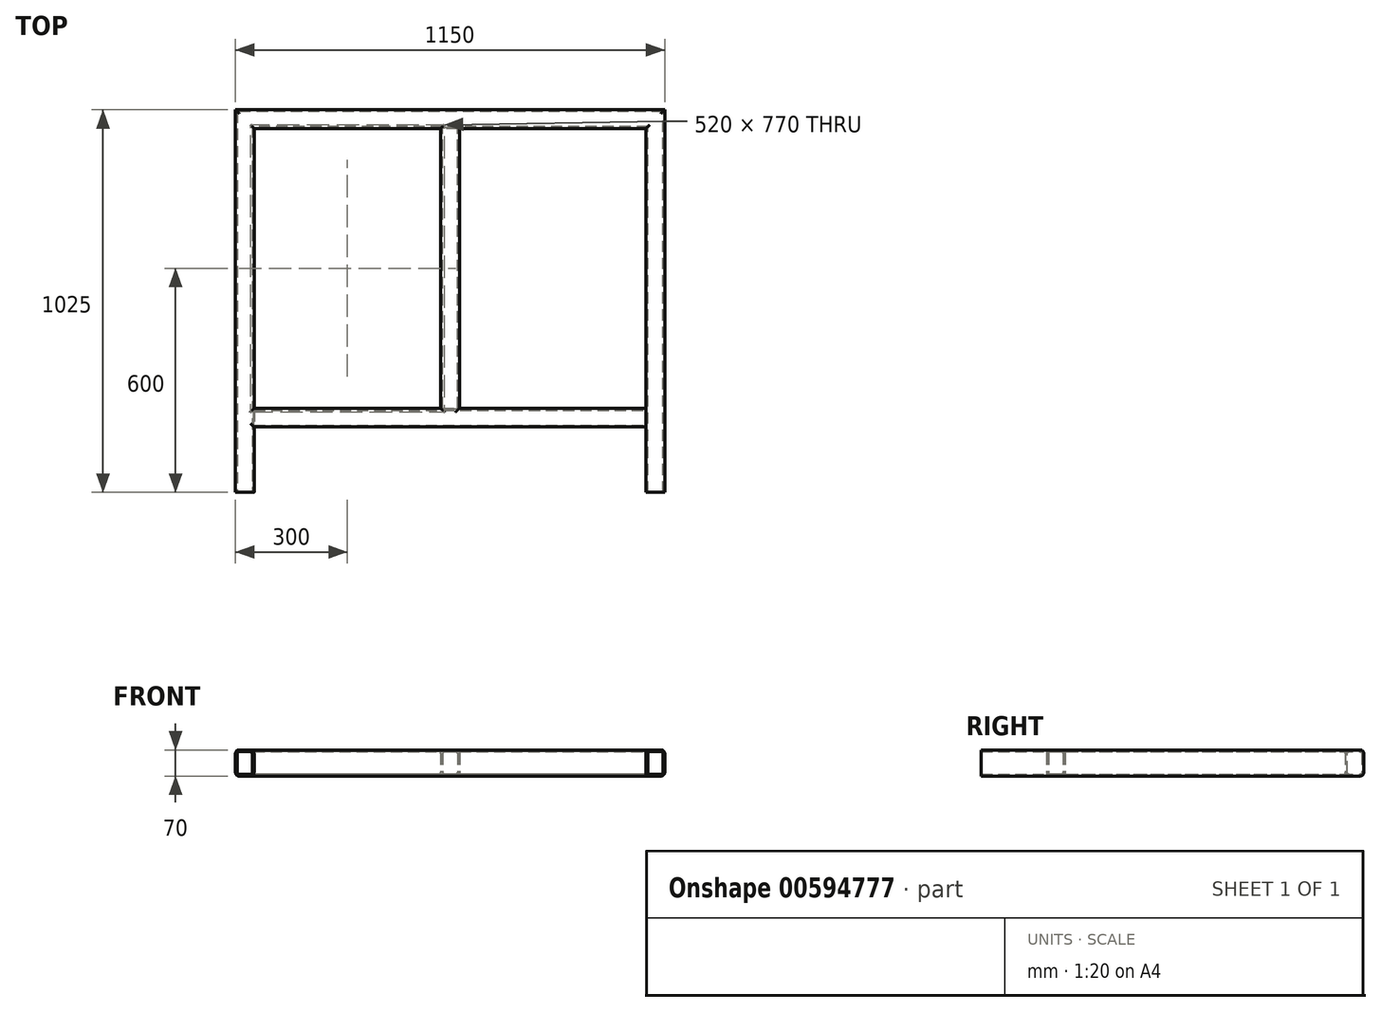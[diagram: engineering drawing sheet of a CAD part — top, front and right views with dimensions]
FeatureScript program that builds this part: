
annotation { "Feature Type Name" : "Feature", "Feature Type Description" : "" }
export const myFeature = defineFeature(function(context is Context, id is Id, definition is map)
    precondition{}
    {
        {
            var Q0;
            Q0=qCreatedBy(makeId("Top.planeOp"),FACE);
            var sketch = newSketch(context, id + "F0", { "sketchPlane" : qUnion([Q0])});
            skLineSegment(sketch, "E0", {"start": v(0, 0) * mm, "end": v(0, 1000) * mm});
            skLineSegment(sketch, "E1", {"start": v(0, 1000) * mm, "end": v(-1100, 1000) * mm});
            skLineSegment(sketch, "E2", {"start": v(-1100, 1000) * mm, "end": v(-1100, 0) * mm});
            skLineSegment(sketch, "E3", {"start": v(-1100, 200) * mm, "end": v(0, 200) * mm});
            skLineSegment(sketch, "E4", {"start": v(-550, 1000) * mm, "end": v(-550, 200) * mm});
            skSolve(sketch);
        }
        {
            var Q0;
            Q0=qCreatedBy(makeId("Front.planeOp"),FACE);
            var sketch = newSketch(context, id + "F1", { "sketchPlane" : qUnion([Q0])});
            skLineSegment(sketch, "E5.bottom", {"start": v(15, 35) * mm, "end": v(-15, 35) * mm});
            skLineSegment(sketch, "E5.top", {"start": v(15, -35) * mm, "end": v(-15, -35) * mm});
            skLineSegment(sketch, "E5.left", {"start": v(25, 25) * mm, "end": v(25, -25) * mm});
            skLineSegment(sketch, "E5.right", {"start": v(-25, 25) * mm, "end": v(-25, -25) * mm});
            skPoint(sketch, "E5.middle", {"position": v(0, 0) * mm});
            skPoint(sketch, "E6.visualSharp", {"position": v(-25, 35) * mm});
            skArc(sketch, "E6.filletArc", {"start": v(-15, 35) * mm, "mid": v(-22.07, 32.07) * mm, "end": v(-25, 25) * mm});
            skPoint(sketch, "E7.visualSharp", {"position": v(25, 35) * mm});
            skArc(sketch, "E7.filletArc", {"start": v(25, 25) * mm, "mid": v(22.07, 32.07) * mm, "end": v(15, 35) * mm});
            skPoint(sketch, "E8.visualSharp", {"position": v(-25, -35) * mm});
            skArc(sketch, "E8.filletArc", {"start": v(-25, -25) * mm, "mid": v(-22.07, -32.07) * mm, "end": v(-15, -35) * mm});
            skPoint(sketch, "E9.visualSharp", {"position": v(25, -35) * mm});
            skArc(sketch, "E9.filletArc", {"start": v(15, -35) * mm, "mid": v(22.07, -32.07) * mm, "end": v(25, -25) * mm});
            skArc(sketch, "E10.0", {"start": v(-15, 30) * mm, "mid": v(-18.54, 28.54) * mm, "end": v(-20, 25) * mm});
            skLineSegment(sketch, "E10.1", {"start": v(15, 30) * mm, "end": v(-15, 30) * mm});
            skLineSegment(sketch, "E10.2", {"start": v(-20, 25) * mm, "end": v(-20, -25) * mm});
            skArc(sketch, "E10.3", {"start": v(20, 25) * mm, "mid": v(18.54, 28.54) * mm, "end": v(15, 30) * mm});
            skArc(sketch, "E10.4", {"start": v(-20, -25) * mm, "mid": v(-18.54, -28.54) * mm, "end": v(-15, -30) * mm});
            skLineSegment(sketch, "E10.5", {"start": v(15, -30) * mm, "end": v(-15, -30) * mm});
            skArc(sketch, "E10.6", {"start": v(15, -30) * mm, "mid": v(18.54, -28.54) * mm, "end": v(20, -25) * mm});
            skLineSegment(sketch, "E10.7", {"start": v(20, 25) * mm, "end": v(20, -25) * mm});
            skSolve(sketch);
        }
        {
            var Q0;
            Q0=makeQuery(id+"F1.imprint","IMPRINT",FACE,{"disambiguationData":[TD([[makeQuery(id+"F1.imprint","IMPRINT",EDGE,{"derivedFrom":sQuery(id+"F1.wireOp",EDGE,"E5.bottom")}),1.0]])]});
            var Q1;
            Q1=sQuery(id+"F0.wireOp",EDGE,"E0");
            var Q2;
            Q2=sQuery(id+"F0.wireOp",EDGE,"E1");
            var Q3;
            Q3=sQuery(id+"F0.wireOp",EDGE,"E2");
            sweep(context, id + "F2", {"profiles" : qUnion([Q0]), "path" : qUnion([Q1, Q2, Q3])});
        }
        {
            var Q0;
            Q0=makeQuery(id+"F2.opSweep","SWEPT_FACE",FACE,{"disambiguationData":[OSD([sQuery(id+"F0.wireOp",EDGE,"E0"),sQuery(id+"F1.wireOp",EDGE,"E5.right")])]});
            var sketch = newSketch(context, id + "F3", { "sketchPlane" : qUnion([Q0])});
            skLineSegment(sketch, "E11.bottom", {"start": v(-185, 35) * mm, "end": v(-215, 35) * mm});
            skLineSegment(sketch, "E11.top", {"start": v(-185, -35) * mm, "end": v(-215, -35) * mm});
            skLineSegment(sketch, "E11.left", {"start": v(-175, 25) * mm, "end": v(-175, -25) * mm});
            skLineSegment(sketch, "E11.right", {"start": v(-225, 25) * mm, "end": v(-225, -25) * mm});
            skPoint(sketch, "E11.middle", {"position": v(-200, 0) * mm});
            skPoint(sketch, "E12.visualSharp", {"position": v(-225, 35) * mm});
            skArc(sketch, "E12.filletArc", {"start": v(-215, 35) * mm, "mid": v(-222.07, 32.07) * mm, "end": v(-225, 25) * mm});
            skPoint(sketch, "E13.visualSharp", {"position": v(-175, 35) * mm});
            skArc(sketch, "E13.filletArc", {"start": v(-175, 25) * mm, "mid": v(-177.93, 32.07) * mm, "end": v(-185, 35) * mm});
            skPoint(sketch, "E14.visualSharp", {"position": v(-225, -35) * mm});
            skArc(sketch, "E14.filletArc", {"start": v(-225, -25) * mm, "mid": v(-222.07, -32.07) * mm, "end": v(-215, -35) * mm});
            skPoint(sketch, "E15.visualSharp", {"position": v(-175, -35) * mm});
            skArc(sketch, "E15.filletArc", {"start": v(-185, -35) * mm, "mid": v(-177.93, -32.07) * mm, "end": v(-175, -25) * mm});
            skArc(sketch, "E16.0", {"start": v(-215, 30) * mm, "mid": v(-218.54, 28.54) * mm, "end": v(-220, 25) * mm});
            skLineSegment(sketch, "E16.1", {"start": v(-185, 30) * mm, "end": v(-215, 30) * mm});
            skLineSegment(sketch, "E16.2", {"start": v(-220, 25) * mm, "end": v(-220, -25) * mm});
            skArc(sketch, "E16.3", {"start": v(-180, 25) * mm, "mid": v(-181.46, 28.54) * mm, "end": v(-185, 30) * mm});
            skArc(sketch, "E16.4", {"start": v(-220, -25) * mm, "mid": v(-218.54, -28.54) * mm, "end": v(-215, -30) * mm});
            skLineSegment(sketch, "E16.5", {"start": v(-185, -30) * mm, "end": v(-215, -30) * mm});
            skArc(sketch, "E16.6", {"start": v(-185, -30) * mm, "mid": v(-181.46, -28.54) * mm, "end": v(-180, -25) * mm});
            skLineSegment(sketch, "E16.7", {"start": v(-180, 25) * mm, "end": v(-180, -25) * mm});
            skSolve(sketch);
        }
        {
            var Q0;
            Q0=makeQuery(id+"F3.imprint","IMPRINT",FACE,{"disambiguationData":[TD([[makeQuery(id+"F3.imprint","IMPRINT",EDGE,{"derivedFrom":sQuery(id+"F3.wireOp",EDGE,"E11.bottom")}),1.0]])]});
            var Q1;
            {var subQ0=sQuery(id+"F3.wireOp",EDGE,"E11.left");Q1=makeQuery(id+"F3.imprint","IMPRINT",FACE,{"disambiguationData":[TD([[makeQuery(id+"F3.imprint","IMPRINT",EDGE,{"derivedFrom":subQ0}),-1.0]])]});}
            var Q2;
            Q2=makeQuery(id+"F3.imprint","IMPRINT",FACE,{"disambiguationData":[TD([[makeQuery(id+"F3.imprint","IMPRINT",EDGE,{"derivedFrom":sQuery(id+"F3.wireOp",EDGE,"E11.top")}),-1.0]])]});
            var Q3;
            {var subQ0=sQuery(id+"F3.wireOp",EDGE,"E11.right");Q3=makeQuery(id+"F3.imprint","IMPRINT",FACE,{"disambiguationData":[TD([[makeQuery(id+"F3.imprint","IMPRINT",EDGE,{"derivedFrom":subQ0}),1.0]])]});}
            extrude(context, id + "F4", {"entities" : qUnion([Q0, Q1, Q2, Q3]), "operationType" : NewBodyOperationType.ADD, "endBound" : BoundingType.UP_TO_NEXT, "depth" : 25 * mm, "offsetDistance" : 25 * mm});
        }
        {
            var Q0;
            Q0=sQuery(id+"F0.wireOp",EDGE,"E4");
            cPoint(context, id + "F5", {"entities" : qUnion([Q0]), "parameter" : 0.5});
        }
        {
            var Q0;
            Q0 = qCreatedBy(id + "F5" ,VERTEX);
            var Q1;
            Q1=qCreatedBy(makeId("Front.planeOp"),FACE);
            cPlane(context, id + "F6", {"entities" : qUnion([Q0, Q1]), "cplaneType" : CPlaneType.PLANE_POINT, "offset" : 0 * mm, "width" : 150 * mm, "height" : 150 * mm});
        }
        {
            var Q0;
            Q0=qCreatedBy(id+"F6.planeOp",FACE);
            var sketch = newSketch(context, id + "F7", { "sketchPlane" : qUnion([Q0])});
            skLineSegment(sketch, "E17.bottom", {"start": v(-535, 35) * mm, "end": v(-565, 35) * mm});
            skLineSegment(sketch, "E17.top", {"start": v(-535, -35) * mm, "end": v(-565, -35) * mm});
            skLineSegment(sketch, "E17.left", {"start": v(-525, 25) * mm, "end": v(-525, -25) * mm});
            skLineSegment(sketch, "E17.right", {"start": v(-575, 25) * mm, "end": v(-575, -25) * mm});
            skPoint(sketch, "E17.middle", {"position": v(-550, 0) * mm});
            skPoint(sketch, "E18.visualSharp", {"position": v(-575, 35) * mm});
            skArc(sketch, "E18.filletArc", {"start": v(-565, 35) * mm, "mid": v(-572.07, 32.07) * mm, "end": v(-575, 25) * mm});
            skPoint(sketch, "E19.visualSharp", {"position": v(-525, 35) * mm});
            skArc(sketch, "E19.filletArc", {"start": v(-525, 25) * mm, "mid": v(-527.93, 32.07) * mm, "end": v(-535, 35) * mm});
            skPoint(sketch, "E20.visualSharp", {"position": v(-575, -35) * mm});
            skArc(sketch, "E20.filletArc", {"start": v(-575, -25) * mm, "mid": v(-572.07, -32.07) * mm, "end": v(-565, -35) * mm});
            skPoint(sketch, "E21.visualSharp", {"position": v(-525, -35) * mm});
            skArc(sketch, "E21.filletArc", {"start": v(-535, -35) * mm, "mid": v(-527.93, -32.07) * mm, "end": v(-525, -25) * mm});
            skArc(sketch, "E22.0", {"start": v(-530, 25) * mm, "mid": v(-531.46, 28.54) * mm, "end": v(-535, 30) * mm});
            skLineSegment(sketch, "E22.1", {"start": v(-530, 25) * mm, "end": v(-530, -25) * mm});
            skLineSegment(sketch, "E22.2", {"start": v(-535, 30) * mm, "end": v(-565, 30) * mm});
            skArc(sketch, "E22.3", {"start": v(-535, -30) * mm, "mid": v(-531.46, -28.54) * mm, "end": v(-530, -25) * mm});
            skArc(sketch, "E22.4", {"start": v(-565, 30) * mm, "mid": v(-568.54, 28.54) * mm, "end": v(-570, 25) * mm});
            skLineSegment(sketch, "E22.5", {"start": v(-570, 25) * mm, "end": v(-570, -25) * mm});
            skArc(sketch, "E22.6", {"start": v(-570, -25) * mm, "mid": v(-568.54, -28.54) * mm, "end": v(-565, -30) * mm});
            skLineSegment(sketch, "E22.7", {"start": v(-535, -30) * mm, "end": v(-565, -30) * mm});
            skSolve(sketch);
        }
        {
            var Q0;
            Q0=makeQuery(id+"F7.imprint","IMPRINT",FACE,{"disambiguationData":[TD([[makeQuery(id+"F7.imprint","IMPRINT",EDGE,{"derivedFrom":sQuery(id+"F7.wireOp",EDGE,"E17.bottom")}),1.0]])]});
            extrude(context, id + "F8", {"entities" : qUnion([Q0]), "operationType" : NewBodyOperationType.ADD, "endBound" : BoundingType.UP_TO_NEXT, "depth" : 25 * mm, "offsetDistance" : 25 * mm, "hasSecondDirection" : true, "secondDirectionBound" : BoundingType.UP_TO_NEXT, "secondDirectionOppositeDirection" : true, "secondDirectionDepth" : 25 * mm});
        }
    });
